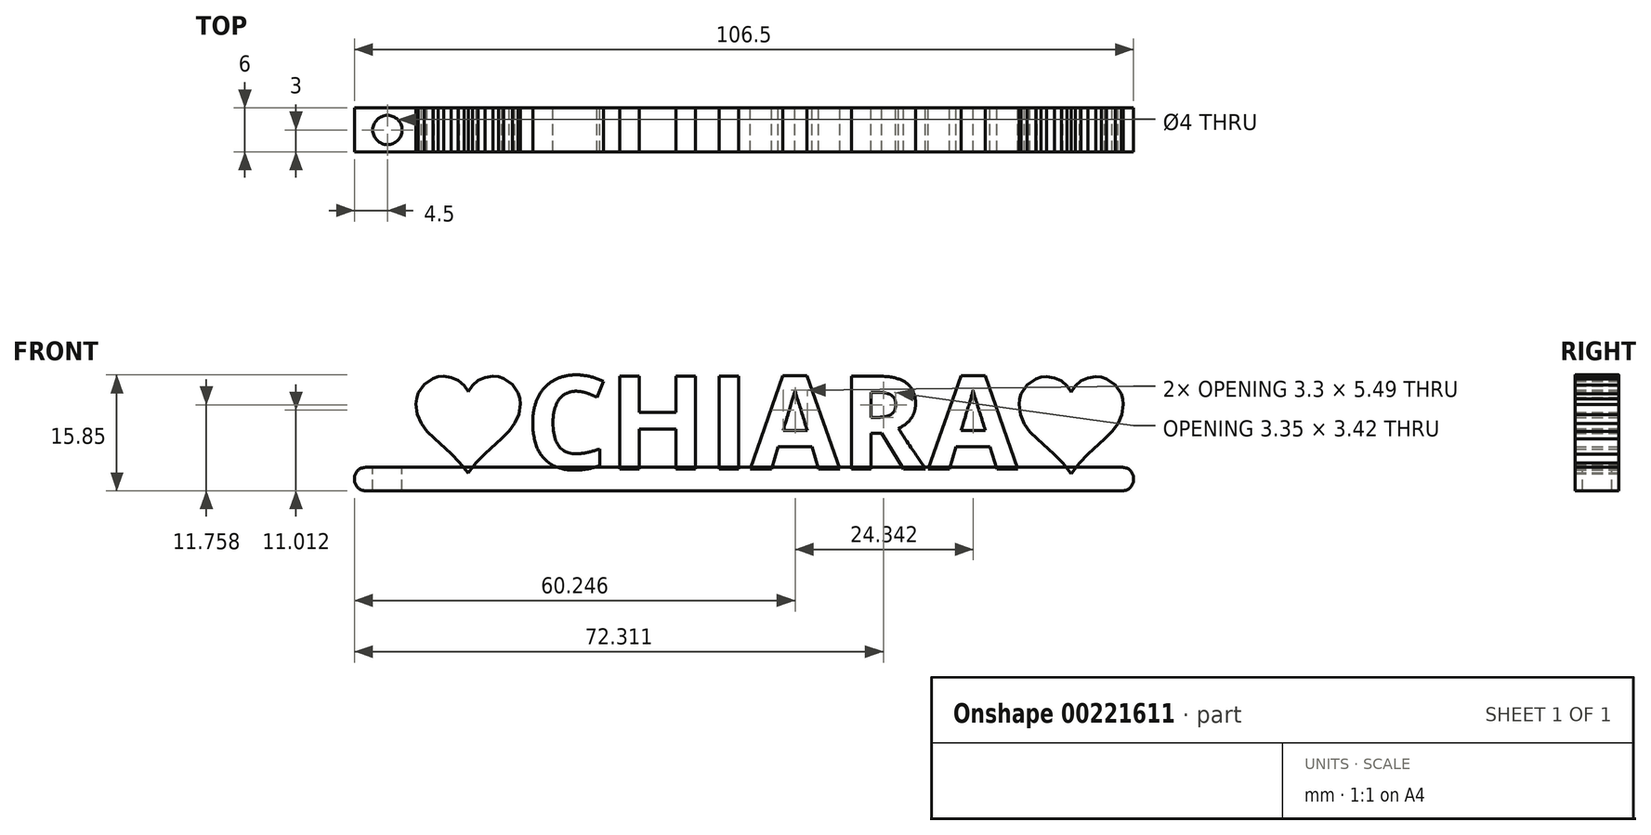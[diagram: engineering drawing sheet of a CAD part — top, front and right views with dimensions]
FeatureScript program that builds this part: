
annotation { "Feature Type Name" : "Feature", "Feature Type Description" : "" }
export const myFeature = defineFeature(function(context is Context, id is Id, definition is map)
    precondition{}
    {
        {
            var Q0;
            Q0=qCreatedBy(makeId("Front.planeOp"),FACE);
            var sketch = newSketch(context, id + "F0", { "sketchPlane" : qUnion([Q0])});
            skText(sketch, "E0", { "text": "   CHIARA", "fontName": "OpenSans-Bold.ttf"});
            skLineSegment(sketch, "E1", {"start": v(66.12, 12.6) * mm, "end": v(65.36, 12.52) * mm});
            skLineSegment(sketch, "E2", {"start": v(65.36, 12.52) * mm, "end": v(64.66, 12.3) * mm});
            skLineSegment(sketch, "E3", {"start": v(64.66, 12.3) * mm, "end": v(63.46, 11.5) * mm});
            skLineSegment(sketch, "E4", {"start": v(63.46, 11.5) * mm, "end": v(62.65, 10.3) * mm});
            skLineSegment(sketch, "E5", {"start": v(62.65, 10.3) * mm, "end": v(62.43, 9.59) * mm});
            skLineSegment(sketch, "E6", {"start": v(62.43, 9.59) * mm, "end": v(62.36, 8.83) * mm});
            skLineSegment(sketch, "E7", {"start": v(62.36, 8.83) * mm, "end": v(62.54, 7.39) * mm});
            skLineSegment(sketch, "E8", {"start": v(62.54, 7.39) * mm, "end": v(63.07, 6.16) * mm});
            skLineSegment(sketch, "E9", {"start": v(63.07, 6.16) * mm, "end": v(63.85, 5.08) * mm});
            skLineSegment(sketch, "E10", {"start": v(63.85, 5.08) * mm, "end": v(64.83, 4.08) * mm});
            skLineSegment(sketch, "E11", {"start": v(64.83, 4.08) * mm, "end": v(67.13, 2.03) * mm});
            skLineSegment(sketch, "E12", {"start": v(67.13, 2.03) * mm, "end": v(68.32, 0.82) * mm});
            skLineSegment(sketch, "E13", {"start": v(68.32, 0.82) * mm, "end": v(69.44, -0.59) * mm});
            skLineSegment(sketch, "E14", {"start": v(69.44, -0.59) * mm, "end": v(69.48, -0.65) * mm});
            skLineSegment(sketch, "E15", {"start": v(69.48, -0.65) * mm, "end": v(69.53, -0.59) * mm});
            skLineSegment(sketch, "E16", {"start": v(69.53, -0.59) * mm, "end": v(70.6, 0.82) * mm});
            skLineSegment(sketch, "E17", {"start": v(70.6, 0.82) * mm, "end": v(71.77, 2.03) * mm});
            skLineSegment(sketch, "E18", {"start": v(71.77, 2.03) * mm, "end": v(74.07, 4.12) * mm});
            skLineSegment(sketch, "E19", {"start": v(74.07, 4.12) * mm, "end": v(75.07, 5.13) * mm});
            skLineSegment(sketch, "E20", {"start": v(75.07, 5.13) * mm, "end": v(75.88, 6.21) * mm});
            skLineSegment(sketch, "E21", {"start": v(75.88, 6.21) * mm, "end": v(76.41, 7.42) * mm});
            skLineSegment(sketch, "E22", {"start": v(76.41, 7.42) * mm, "end": v(76.6, 8.83) * mm});
            skLineSegment(sketch, "E23", {"start": v(76.6, 8.83) * mm, "end": v(76.53, 9.59) * mm});
            skLineSegment(sketch, "E24", {"start": v(76.53, 9.59) * mm, "end": v(76.31, 10.3) * mm});
            skLineSegment(sketch, "E25", {"start": v(76.31, 10.3) * mm, "end": v(75.5, 11.5) * mm});
            skLineSegment(sketch, "E26", {"start": v(75.5, 11.5) * mm, "end": v(74.3, 12.3) * mm});
            skLineSegment(sketch, "E27", {"start": v(74.3, 12.3) * mm, "end": v(73.6, 12.52) * mm});
            skLineSegment(sketch, "E28", {"start": v(73.6, 12.52) * mm, "end": v(72.84, 12.6) * mm});
            skLineSegment(sketch, "E29", {"start": v(72.84, 12.6) * mm, "end": v(71.78, 12.44) * mm});
            skLineSegment(sketch, "E30", {"start": v(71.78, 12.44) * mm, "end": v(70.84, 12.01) * mm});
            skLineSegment(sketch, "E31", {"start": v(70.84, 12.01) * mm, "end": v(70.06, 11.35) * mm});
            skLineSegment(sketch, "E32", {"start": v(70.06, 11.35) * mm, "end": v(69.48, 10.5) * mm});
            skLineSegment(sketch, "E33", {"start": v(69.48, 10.5) * mm, "end": v(68.9, 11.35) * mm});
            skLineSegment(sketch, "E34", {"start": v(68.9, 11.35) * mm, "end": v(68.12, 12.01) * mm});
            skLineSegment(sketch, "E35", {"start": v(68.12, 12.01) * mm, "end": v(67.18, 12.44) * mm});
            skLineSegment(sketch, "E36", {"start": v(67.18, 12.44) * mm, "end": v(66.12, 12.6) * mm});
            skLineSegment(sketch, "E37", {"start": v(63, 12.78) * mm, "end": v(73.76, 12.78) * mm, "construction": true});
            skLineSegment(sketch, "E38", {"start": v(-16.32, 12.66) * mm, "end": v(-17.08, 12.59) * mm});
            skLineSegment(sketch, "E39", {"start": v(-17.08, 12.59) * mm, "end": v(-17.78, 12.37) * mm});
            skLineSegment(sketch, "E40", {"start": v(-17.78, 12.37) * mm, "end": v(-18.98, 11.56) * mm});
            skLineSegment(sketch, "E41", {"start": v(-18.98, 11.56) * mm, "end": v(-19.79, 10.36) * mm});
            skLineSegment(sketch, "E42", {"start": v(-19.79, 10.36) * mm, "end": v(-20, 9.65) * mm});
            skLineSegment(sketch, "E43", {"start": v(-20, 9.65) * mm, "end": v(-20.09, 8.9) * mm});
            skLineSegment(sketch, "E44", {"start": v(-20.09, 8.9) * mm, "end": v(-19.9, 7.45) * mm});
            skLineSegment(sketch, "E45", {"start": v(-19.9, 7.45) * mm, "end": v(-19.38, 6.22) * mm});
            skLineSegment(sketch, "E46", {"start": v(-19.38, 6.22) * mm, "end": v(-18.6, 5.15) * mm});
            skLineSegment(sketch, "E47", {"start": v(-18.6, 5.15) * mm, "end": v(-17.6, 4.15) * mm});
            skLineSegment(sketch, "E48", {"start": v(-17.6, 4.15) * mm, "end": v(-15.31, 2.09) * mm});
            skLineSegment(sketch, "E49", {"start": v(-15.31, 2.09) * mm, "end": v(-14.13, 0.89) * mm});
            skLineSegment(sketch, "E50", {"start": v(-14.13, 0.89) * mm, "end": v(-13, -0.52) * mm});
            skLineSegment(sketch, "E51", {"start": v(-13, -0.52) * mm, "end": v(-12.96, -0.59) * mm});
            skLineSegment(sketch, "E52", {"start": v(-12.96, -0.59) * mm, "end": v(-12.92, -0.52) * mm});
            skLineSegment(sketch, "E53", {"start": v(-12.92, -0.52) * mm, "end": v(-11.84, 0.89) * mm});
            skLineSegment(sketch, "E54", {"start": v(-11.84, 0.89) * mm, "end": v(-10.67, 2.1) * mm});
            skLineSegment(sketch, "E55", {"start": v(-10.67, 2.1) * mm, "end": v(-8.37, 4.19) * mm});
            skLineSegment(sketch, "E56", {"start": v(-8.37, 4.19) * mm, "end": v(-7.37, 5.2) * mm});
            skLineSegment(sketch, "E57", {"start": v(-7.37, 5.2) * mm, "end": v(-6.56, 6.28) * mm});
            skLineSegment(sketch, "E58", {"start": v(-6.56, 6.28) * mm, "end": v(-6.03, 7.49) * mm});
            skLineSegment(sketch, "E59", {"start": v(-6.03, 7.49) * mm, "end": v(-5.83, 8.9) * mm});
            skLineSegment(sketch, "E60", {"start": v(-5.83, 8.9) * mm, "end": v(-5.91, 9.65) * mm});
            skLineSegment(sketch, "E61", {"start": v(-5.91, 9.65) * mm, "end": v(-6.13, 10.36) * mm});
            skLineSegment(sketch, "E62", {"start": v(-6.13, 10.36) * mm, "end": v(-6.94, 11.56) * mm});
            skLineSegment(sketch, "E63", {"start": v(-6.94, 11.56) * mm, "end": v(-8.13, 12.37) * mm});
            skLineSegment(sketch, "E64", {"start": v(-8.13, 12.37) * mm, "end": v(-8.84, 12.59) * mm});
            skLineSegment(sketch, "E65", {"start": v(-8.84, 12.59) * mm, "end": v(-9.6, 12.66) * mm});
            skLineSegment(sketch, "E66", {"start": v(-9.6, 12.66) * mm, "end": v(-10.66, 12.5) * mm});
            skLineSegment(sketch, "E67", {"start": v(-10.66, 12.5) * mm, "end": v(-11.6, 12.08) * mm});
            skLineSegment(sketch, "E68", {"start": v(-11.6, 12.08) * mm, "end": v(-12.38, 11.41) * mm});
            skLineSegment(sketch, "E69", {"start": v(-12.38, 11.41) * mm, "end": v(-12.96, 10.56) * mm});
            skLineSegment(sketch, "E70", {"start": v(-12.96, 10.56) * mm, "end": v(-13.54, 11.41) * mm});
            skLineSegment(sketch, "E71", {"start": v(-13.54, 11.41) * mm, "end": v(-14.32, 12.08) * mm});
            skLineSegment(sketch, "E72", {"start": v(-14.32, 12.08) * mm, "end": v(-15.26, 12.5) * mm});
            skLineSegment(sketch, "E73", {"start": v(-15.26, 12.5) * mm, "end": v(-16.32, 12.66) * mm});
            const initialGuessF0  = {"E0": [-0.019, 0, 1, 0, 0.01278]};
            skSetInitialGuess(sketch, initialGuessF0);
            skSolve(sketch);
        }
        {
            var Q0;
            Q0=qSketchRegion(id+"F0",true);
            extrude(context, id + "F1", {"entities" : qUnion([Q0]), "endBound" : BoundingType.SYMMETRIC, "depth" : 6 * mm});
        }
        {
            var Q0;
            Q0=qCreatedBy(makeId("Top.planeOp"),FACE);
            var sketch = newSketch(context, id + "F2", { "sketchPlane" : qUnion([Q0])});
            skLineSegment(sketch, "E74.bottom", {"start": v(-21, 3) * mm, "end": v(78, 3) * mm});
            skLineSegment(sketch, "E74.top", {"start": v(-21, -3) * mm, "end": v(78, -3) * mm});
            skLineSegment(sketch, "E74.left", {"start": v(-21, 3) * mm, "end": v(-21, -3) * mm});
            skLineSegment(sketch, "E74.right", {"start": v(78, 3) * mm, "end": v(78, -3) * mm});
            skSolve(sketch);
        }
        {
            var Q0;
            Q0=makeQuery(id+"F2.imprint","IMPRINT",FACE,{"disambiguationData":[TD([[makeQuery(id+"F2.imprint","IMPRINT",EDGE,{"derivedFrom":sQuery(id+"F2.wireOp",EDGE,"E74.bottom")}),-1.0]])]});
            extrude(context, id + "F3", {"entities" : qUnion([Q0]), "depth" : 0.2 * mm});
        }
        {
            var Q0;
            Q0=makeQuery(id+"F3.opExtrude","CAP_FACE",FACE,{"disambiguationData":[OSD([sQuery(id+"F2.wireOp",EDGE,"E74.bottom"),sQuery(id+"F2.wireOp",EDGE,"E74.top"),sQuery(id+"F2.wireOp",EDGE,"E74.left"),sQuery(id+"F2.wireOp",EDGE,"E74.right")])],"isStart":true});
            extrude(context, id + "F4", {"entities" : qUnion([Q0]), "depth" : 3 * mm});
        }
        {
            var Q0;
            {var subQ0=sQuery(id+"F2.wireOp",EDGE,"E74.left");Q0=makeQuery(id+"FaVoHrOpcFZXiYX_6.opBoolean","MERGE",FACE,{"derivedFrom":[makeQuery(id+"F3.opExtrude","SWEPT_FACE",FACE,{"disambiguationData":[OSD([subQ0])]}),makeQuery(id+"F4.opExtrude","SWEPT_FACE",FACE,{"disambiguationData":[OSD([subQ0])]})]});}
            var sketch = newSketch(context, id + "F5", { "sketchPlane" : qUnion([Q0])});
            skLineSegment(sketch, "E75.bottom", {"start": v(-3, -3) * mm, "end": v(3, -3) * mm});
            skLineSegment(sketch, "E75.top", {"start": v(-3, 0.2) * mm, "end": v(3, 0.2) * mm});
            skLineSegment(sketch, "E75.left", {"start": v(-3, -3) * mm, "end": v(-3, 0.2) * mm});
            skLineSegment(sketch, "E75.right", {"start": v(3, -3) * mm, "end": v(3, 0.2) * mm});
            skSolve(sketch);
        }
        {
            var Q0;
            Q0=qSketchRegion(id+"F5",true);
            extrude(context, id + "F6", {"entities" : qUnion([Q0]), "operationType" : NewBodyOperationType.ADD, "depth" : 7.5 * mm});
        }
        {
            var Q0;
            Q0=makeQuery(id+"F6.opExtrude","CAP_EDGE",EDGE,{"disambiguationData":[OSD([sQuery(id+"F5.wireOp",EDGE,"E75.bottom")])],"isStart":false});
            var Q1;
            Q1=makeQuery(id+"F6.opExtrude","CAP_EDGE",EDGE,{"disambiguationData":[OSD([sQuery(id+"F5.wireOp",EDGE,"E75.top")])],"isStart":false});
            var Q2;
            Q2=makeQuery(id+"F4.opExtrude","CAP_EDGE",EDGE,{"disambiguationData":[OSD([sQuery(id+"F2.wireOp",EDGE,"E74.right")])],"isStart":false});
            fillet(context, id + "F7", {"entities" : qUnion([Q0, Q1, Q2]), "radius" : 1.5 * mm, "tangentPropagation" : true, "allowEdgeOverflow" : false});
        }
        {
            var Q0;
            {var subQ19=sQuery(id+"F2.wireOp",EDGE,"E74.top");var subQ20=sQuery(id+"F2.wireOp",EDGE,"E74.bottom");var subQ63=sQuery(id+"F0.wireOp",EDGE,"E0.sketch_text.stroke-2");var subQ66=sQuery(id+"F2.wireOp",EDGE,"E74.left");Q0=makeQuery(id+"F6.boolean.opBoolean","MERGE",FACE,{"derivedFrom":[makeQuery(id+"FaVoHrOpcFZXiYX_6.opBoolean","SPLIT",FACE,{"disambiguationData":[TD([makeQuery(id+"F1.opExtrude","SWEPT_FACE",FACE,{"disambiguationData":[OSD([subQ63])]})])],"derivedFrom":makeQuery(id+"F3.opExtrude","CAP_FACE",FACE,{"disambiguationData":[OSD([subQ20,subQ19,subQ66,sQuery(id+"F2.wireOp",EDGE,"E74.right")])],"isStart":false})}),makeQuery(id+"F6.opExtrude","SWEPT_FACE",FACE,{"disambiguationData":[OSD([sQuery(id+"F5.wireOp",EDGE,"E75.top")])]})]});}
            var sketch = newSketch(context, id + "F8", { "sketchPlane" : qUnion([Q0])});
            skCircle(sketch, "E76", {"center": v(-24, 0) * mm, "radius": 2 * mm});
            skSolve(sketch);
        }
        {
            var Q0;
            Q0=makeQuery(id+"F8.imprint","IMPRINT",FACE,{"disambiguationData":[TD([[makeQuery(id+"F8.imprint","IMPRINT",EDGE,{"derivedFrom":sQuery(id+"F8.wireOp",EDGE,"E76")}),1.0]])]});
            extrude(context, id + "F9", {"entities" : qUnion([Q0]), "operationType" : NewBodyOperationType.REMOVE, "oppositeDirection" : true, "depth" : 4 * mm});
        }
        {
            var Q0;
            Q0=makeQuery(id+"F3.opExtrude","CAP_EDGE",EDGE,{"disambiguationData":[OSD([sQuery(id+"F2.wireOp",EDGE,"E74.right")])],"isStart":false});
            fillet(context, id + "F10", {"entities" : qUnion([Q0]), "radius" : 1.5 * mm, "tangentPropagation" : true, "allowEdgeOverflow" : false});
        }
    });
